# Revit family: Dock_Shelter_Nova-Tech_RF
name_source: partatom
category: Generic Models
revit_build: Autodesk Revit 2017 (Build: 20160225_1515(x64)
units: mm (PartAtom-declared; Revit-internal decimal feet)

## family parameters
Always vertical = No
Can host rebar = No
Cut with Voids When Loaded = No
OmniClass Number = 23.50.70.24
OmniClass Title = Seals and Shelters
Part Type = Normal
Room Calculation Point = No
Round Connector Dimension = Use Diameter
Shared = No
Work Plane-Based = Yes

## types (1)
- Dock_Shelter_Nova-Tech_RF
    Assembly Code = E1030300
    Default Elevation = 4' - 0"
    Description = Nova Technology Dock Seal as Specified
    Expected Lifespan (Years) = 0
    Guide Color = Polyethylene Sheeting - Yellow
    Header Height = 0' - 0"
    Keynote = 11160
    Maintenance Schedule (Months) = 0
    Manufacturer = Nova Technology
    Manufacturer Fax = 262-502-1511
    Manufacturer Website = http://www.novalocks.com
    Material = Polyethylene Sheeting - Black
    Model = As Specified
    Opening Height Maximum = 12' - 0"
    Opening Height Minimum = 3' - 0"
    Opening Width Maximum = 8' - 6"
    Opening Width Minimum = 6' - 6"
    Panel Width_Back = 0' - 3 5/8"
    Product Data = http://arcat.com
    Revision = R1_02-2013
    Sales Information = http://www.novalocks.com
    Send Message = http://www.arcat.com
    Specification = http://arcat.com
    URL = http://www.novalocks.com
    Warranty Duration (Years) = 0

## geometry (parser evidence)
native form markers: Blend x8, Sweep x6
no freeform markers — native parametric forms only
